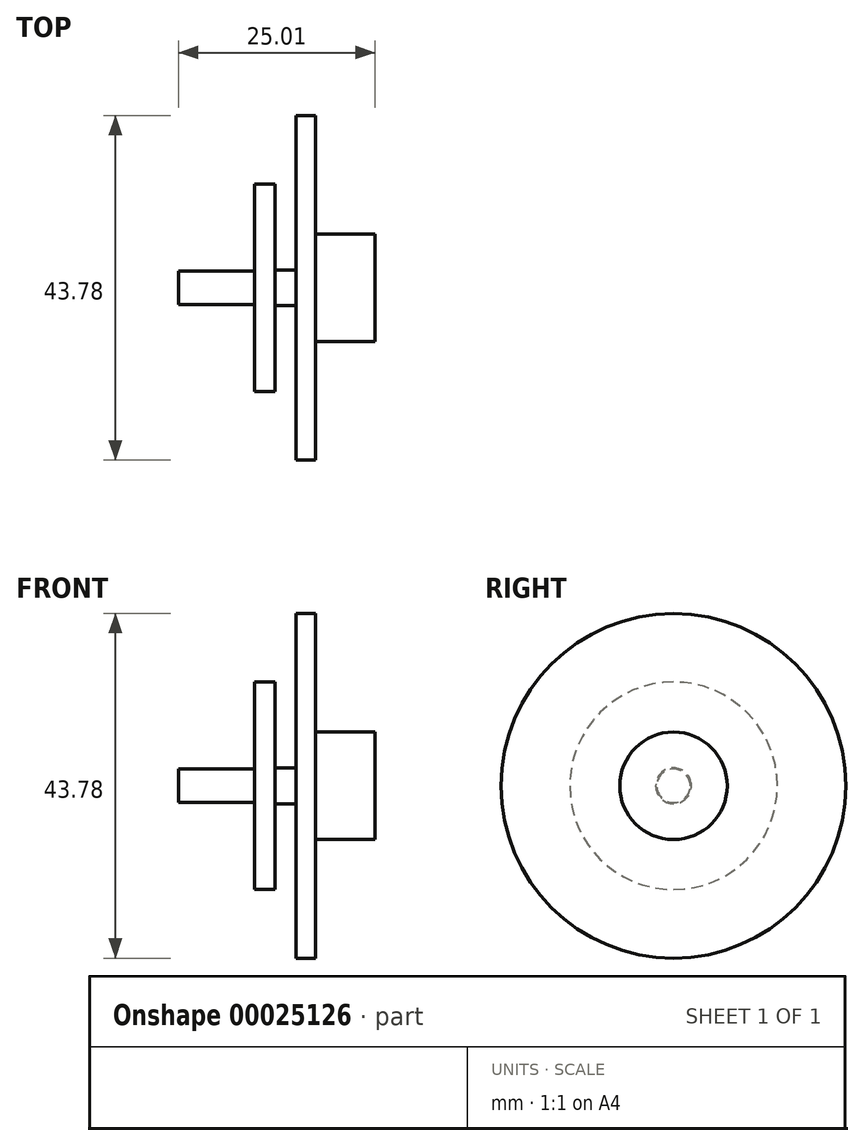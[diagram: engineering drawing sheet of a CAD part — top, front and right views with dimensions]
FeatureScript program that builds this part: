
annotation { "Feature Type Name" : "Feature", "Feature Type Description" : "" }
export const myFeature = defineFeature(function(context is Context, id is Id, definition is map)
    precondition{}
    {
        {
            var Q0;
            Q0=qCreatedBy(makeId("Front.planeOp"),FACE);
            var sketch = newSketch(context, id + "F0", { "sketchPlane" : qUnion([Q0])});
            skLineSegment(sketch, "E0", {"start": v(-35.48, 0) * mm, "end": v(-35.48, 2.13) * mm});
            skLineSegment(sketch, "E1", {"start": v(-35.48, 2.13) * mm, "end": v(-25.81, 2.13) * mm});
            skLineSegment(sketch, "E2", {"start": v(-25.81, 2.13) * mm, "end": v(-25.81, 13.19) * mm});
            skLineSegment(sketch, "E3", {"start": v(-25.81, 13.19) * mm, "end": v(-23.19, 13.19) * mm});
            skLineSegment(sketch, "E4", {"start": v(-23.19, 13.19) * mm, "end": v(-23.19, 2.27) * mm});
            skLineSegment(sketch, "E5", {"start": v(-23.19, 2.27) * mm, "end": v(-20.56, 2.27) * mm});
            skLineSegment(sketch, "E6", {"start": v(-20.56, 2.27) * mm, "end": v(-20.56, 21.9) * mm});
            skLineSegment(sketch, "E7", {"start": v(-20.56, 21.9) * mm, "end": v(-18.07, 21.9) * mm});
            skLineSegment(sketch, "E8", {"start": v(-18.07, 21.9) * mm, "end": v(-18.07, 6.83) * mm});
            skLineSegment(sketch, "E9", {"start": v(-18.07, 6.83) * mm, "end": v(-10.47, 6.83) * mm});
            skLineSegment(sketch, "E10", {"start": v(-10.47, 6.83) * mm, "end": v(-10.47, 0) * mm});
            skLineSegment(sketch, "E11", {"start": v(-10.47, 0) * mm, "end": v(-35.48, 0) * mm});
            skSolve(sketch);
        }
        {
            var Q0;
            Q0=makeQuery(id+"F0.imprint","IMPRINT",FACE,{"disambiguationData":[TD([[makeQuery(id+"F0.imprint","IMPRINT",EDGE,{"derivedFrom":sQuery(id+"F0.wireOp",EDGE,"E0")}),-1.0]])]});
            var Q1;
            Q1=sQuery(id+"F0.wireOp",EDGE,"E11");
            revolve(context, id + "F1", {"entities" : qUnion([Q0]), "axis" : qUnion([Q1]), "revolveType" : RevolveType.FULL});
        }
    });
